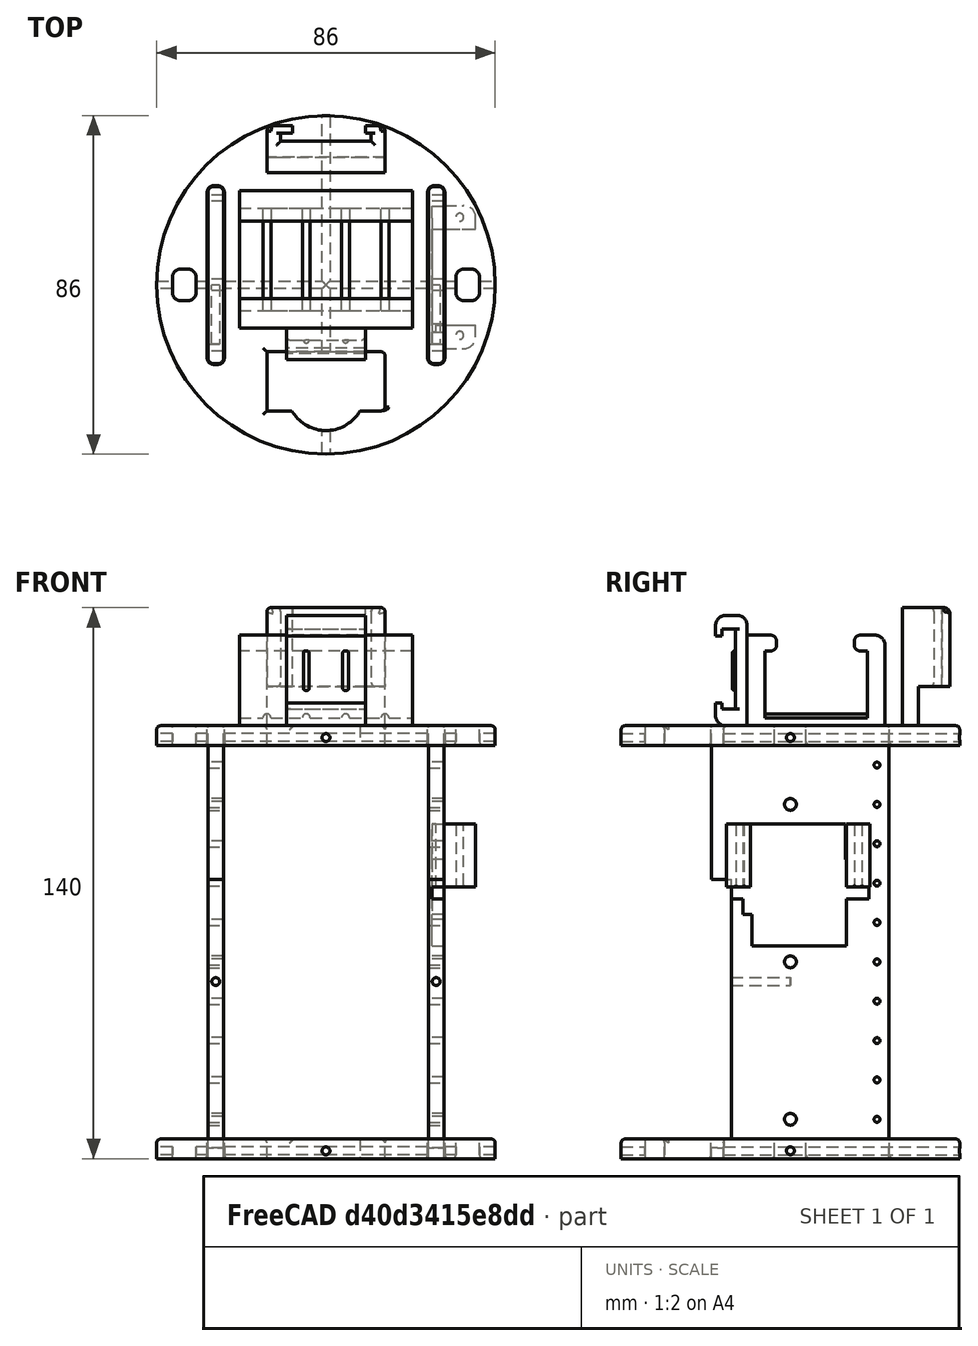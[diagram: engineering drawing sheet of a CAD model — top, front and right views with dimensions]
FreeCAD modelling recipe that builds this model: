
FCSTD DOCUMENT  (FreeCAD 1.0R39109 (Git))
Label: Base_inferior_capsula
License: All rights reserved
LicenseURL: http://en.wikipedia.org/wiki/All_rights_reserved
objects: Part::Cut×130, Part::Cylinder×98, Part::Fillet×96, Part::Box×72, Part::MultiFuse×37, Part::Offset×12, Part::Chamfer×1
note: 446 computed .brp shape members not serialized (recipe doc carries the construction recipe); baked Part::Feature solids carry a one-line shape summary decoded from their .brp

FEATURE [Part::Box] Box  label="Extensor"
  AttacherType = Attacher::AttachEngine3D
  Height = 66
  Length = 11
  Placement = pos=(30,-28,3) rot=(0,0,1;1.5708rad)
  Width = 60
FEATURE [Part::Box] Box001  label="Cubo001"
  AttacherType = Attacher::AttachEngine3D
  Height = 110
  Length = 45
  Placement = pos=(-30,25,0) rot=(0,0,-1;1.5708rad)
  Width = 4
FEATURE [Part::Box] Box002  label="Cubo002"
  AttacherType = Attacher::AttachEngine3D
  Height = 110
  Length = 45
  Placement = pos=(-30,25,0) rot=(0,0,-1;1.5708rad)
  Width = 4
FEATURE [Part::Box] Box003  label="Cubo003"
  AttacherType = Attacher::AttachEngine3D
  Height = 10
  Length = 30
  Placement = pos=(-15,-32,0) rot=(0,0,1;0rad)
  Width = 15
FEATURE [Part::Box] Box005  label="Cubo004"
  AttacherType = Attacher::AttachEngine3D
  Height = 15
  Length = 26
  Placement = pos=(-13,-23,110) rot=(0,0,1;0rad)
  Width = 35
FEATURE [Part::Box] Box006  label="Cubo005"
  AttacherType = Attacher::AttachEngine3D
  Height = 150
  Length = 6
  Width = 8
FEATURE [Part::Box] Box007  label="Cubo006"
  AttacherType = Attacher::AttachEngine3D
  Height = 150
  Length = 6
  Width = 8
FEATURE [Part::Box] Box008  label="Cubo007"
  AttacherType = Attacher::AttachEngine3D
  Height = 150
  Length = 6
  Width = 8
FEATURE [Part::Box] Box009  label="Cubo008"
  AttacherType = Attacher::AttachEngine3D
  Height = 150
  Length = 6
  Width = 8
FEATURE [Part::Box] Box010  label="Cubo009"
  AttacherType = Attacher::AttachEngine3D
  Height = 11.6
  Length = 20.8
  Placement = pos=(-10.5,-23,110) rot=(0,0,1;0rad)
  Width = 35
FEATURE [Part::Box] Box011  label="Cubo010"
  AttacherType = Attacher::AttachEngine3D
  Height = 11.6
  Length = 16
  Placement = pos=(-8,-23,116) rot=(0,0,1;0rad)
  Width = 35
FEATURE [Part::Box] Box095  label="Cubo095"
  AttacherType = Attacher::AttachEngine3D
  Height = 110
  Length = 45
  Placement = pos=(-30,25,0) rot=(0,0,-1;1.5708rad)
  Width = 4
FEATURE [Part::Box] Box096  label="Cubo096"
  AttacherType = Attacher::AttachEngine3D
  Height = 110
  Length = 45
  Placement = pos=(-30,25,0) rot=(0,0,-1;1.5708rad)
  Width = 4
FEATURE [Part::Box] Box097  label="Cubo097"
  AttacherType = Attacher::AttachEngine3D
  Height = 23
  Length = 24
  Width = 14
FEATURE [Part::Box] Box098  label="Cubo098"
  AttacherType = Attacher::AttachEngine3D
  Height = 3
  Length = 33.5
  Placement = pos=(-5,0,16) rot=(0,0,1;0rad)
  Width = 14
FEATURE [Part::Box] Box099  label="Cubo099"
  AttacherType = Attacher::AttachEngine3D
  Height = 1.4
  Length = 13
  Placement = pos=(9.8,5,28.6) rot=(0,0,1;0rad)
  Width = 4
FEATURE [Part::Box] Box100  label="Cubo100"
  AttacherType = Attacher::AttachEngine3D
  Height = 16
  Length = 10
  Placement = pos=(28,12.2,69) rot=(0,0,1;0rad)
  Width = 6
FEATURE [Part::Box] Box101  label="Cubo101"
  AttacherType = Attacher::AttachEngine3D
  Height = 16
  Length = 10
  Placement = pos=(28,-18.2,69) rot=(0,0,1;0rad)
  Width = 6
FEATURE [Part::Box] Box102  label="Extensor001"
  AttacherType = Attacher::AttachEngine3D
  Height = 66
  Length = 11
  Placement = pos=(30,-28,3) rot=(0,0,1;1.5708rad)
  Width = 60
FEATURE [Part::Box] Box104  label="Cubo102"
  AttacherType = Attacher::AttachEngine3D
  Height = 8
  Length = 20
  Width = 28
FEATURE [Part::Box] Box105  label="Cubo103"
  AttacherType = Attacher::AttachEngine3D
  Height = 2
  Length = 20.5
  Placement = pos=(0,4,4) rot=(0,0,1;0rad)
  Width = 20.5
FEATURE [Part::Box] Box106  label="Cubo104"
  AttacherType = Attacher::AttachEngine3D
  Height = 4
  Length = 20.5
  Placement = pos=(0,5,5) rot=(0,0,1;0rad)
  Width = 18.5
FEATURE [Part::Box] Box107  label="Cubo105"
  AttacherType = Attacher::AttachEngine3D
  Height = 8
  Length = 20
  Width = 30
FEATURE [Part::Box] Box108  label="Cubo106"
  AttacherType = Attacher::AttachEngine3D
  Height = 2
  Length = 20.5
  Placement = pos=(0,3.5,4) rot=(0,0,1;0rad)
  Width = 23
FEATURE [Part::Box] Box109  label="Cubo107"
  AttacherType = Attacher::AttachEngine3D
  Height = 4
  Length = 20.5
  Placement = pos=(0,5,5) rot=(0,0,1;0rad)
  Width = 18.5
FEATURE [Part::Box] Box110  label="Cubo108"
  AttacherType = Attacher::AttachEngine3D
  Height = 10
  Length = 20
  Placement = pos=(-9,-38,105) rot=(0,0,1;0rad)
  Width = 15
FEATURE [Part::Box] Box111  label="Cubo109"
  AttacherType = Attacher::AttachEngine3D
  Height = 110
  Length = 45
  Placement = pos=(-30,25,0) rot=(0,0,-1;1.5708rad)
  Width = 4
FEATURE [Part::Box] Box112  label="Extensor003"
  AttacherType = Attacher::AttachEngine3D
  Height = 66
  Length = 11
  Placement = pos=(30,-28,3) rot=(0,0,1;1.5708rad)
  Width = 60
FEATURE [Part::Box] Box113  label="Extensor004"
  AttacherType = Attacher::AttachEngine3D
  Height = 66
  Length = 11
  Placement = pos=(30,-28,3) rot=(0,0,1;1.5708rad)
  Width = 60
FEATURE [Part::Box] Box114  label="Cubo110"
  AttacherType = Attacher::AttachEngine3D
  Height = 110
  Length = 45
  Placement = pos=(-30,25,0) rot=(0,0,-1;1.5708rad)
  Width = 4
FEATURE [Part::Box] Box115  label="Cubo111"
  AttacherType = Attacher::AttachEngine3D
  Height = 23
  Length = 24
  Width = 14
FEATURE [Part::Box] Box116  label="Cubo112"
  AttacherType = Attacher::AttachEngine3D
  Height = 3
  Length = 33.5
  Placement = pos=(-5,0,16) rot=(0,0,1;0rad)
  Width = 14
FEATURE [Part::Box] Box117  label="Cubo113"
  AttacherType = Attacher::AttachEngine3D
  Height = 1.4
  Length = 13
  Placement = pos=(9.8,5,28.6) rot=(0,0,1;0rad)
  Width = 4
FEATURE [Part::Box] Box118  label="Cubo114"
  AttacherType = Attacher::AttachEngine3D
  Height = 16
  Length = 10
  Placement = pos=(28,12.2,69) rot=(0,0,1;0rad)
  Width = 6
FEATURE [Part::Box] Box119  label="Cubo115"
  AttacherType = Attacher::AttachEngine3D
  Height = 16
  Length = 10
  Placement = pos=(28,-18.2,69) rot=(0,0,1;0rad)
  Width = 6
FEATURE [Part::Box] Box120  label="Cubo116"
  AttacherType = Attacher::AttachEngine3D
  Height = 10
  Length = 4
  Placement = pos=(-30,-20,0) rot=(0,0,1;0rad)
  Width = 45
FEATURE [Part::Box] Box121  label="Cubo117"
  AttacherType = Attacher::AttachEngine3D
  Height = 10
  Length = 4
  Placement = pos=(-30,-20,0) rot=(0,0,1;0rad)
  Width = 45
FEATURE [Part::Box] Box122  label="Cubo118"
  AttacherType = Attacher::AttachEngine3D
  Height = 8
  Length = 20
  Width = 30
FEATURE [Part::Box] Box123  label="Cubo119"
  AttacherType = Attacher::AttachEngine3D
  Height = 2
  Length = 20.5
  Placement = pos=(0,3.5,4) rot=(0,0,1;0rad)
  Width = 23
FEATURE [Part::Box] Box124  label="Cubo120"
  AttacherType = Attacher::AttachEngine3D
  Height = 4
  Length = 20.5
  Placement = pos=(0,5,5) rot=(0,0,1;0rad)
  Width = 18.5
FEATURE [Part::Box] Box128  label="Cubo124"
  AttacherType = Attacher::AttachEngine3D
  Height = 30
  Length = 33
  Placement = pos=(-16,-43,115) rot=(0,0,1;0rad)
  Width = 30
FEATURE [Part::Box] Box129  label="Cubo125"
  AttacherType = Attacher::AttachEngine3D
  Height = 30
  Length = 33
  Placement = pos=(-16,13,110) rot=(0,0,1;0rad)
  Width = 30
FEATURE [Part::Box] Box130  label="Cubo126"
  AttacherType = Attacher::AttachEngine3D
  Height = 30
  Length = 30
  Placement = pos=(-16,13,110) rot=(0,0,1;0rad)
  Width = 4
FEATURE [Part::Box] Box131  label="Cubo127"
  AttacherType = Attacher::AttachEngine3D
  Height = 3.4
  Length = 21
  Placement = pos=(0,4.2,3) rot=(0,0,1;0rad)
  Width = 20.4
FEATURE [Part::Box] Box132  label="Cubo128"
  AttacherType = Attacher::AttachEngine3D
  Height = 4
  Length = 21
  Placement = pos=(0,5.75,6) rot=(0,0,1;0rad)
  Width = 17
FEATURE [Part::Box] Box133  label="Cubo129"
  AttacherType = Attacher::AttachEngine3D
  Height = 8
  Length = 20
  Width = 28
FEATURE [Part::Box] Box134  label="Cubo130"
  AttacherType = Attacher::AttachEngine3D
  Height = 16
  Length = 37
  Placement = pos=(-19,-15,110) rot=(0,0,1;0rad)
  Width = 30
FEATURE [Part::Box] Box135  label="Pila_ext"
  AttacherType = Attacher::AttachEngine3D
  Height = 25
  Length = 44
  Placement = pos=(-22,-11,110) rot=(0,0,1;0rad)
  Width = 35
FEATURE [Part::Box] Box136  label="Pila_int"
  AttacherType = Attacher::AttachEngine3D
  Height = 17
  Length = 44
  Placement = pos=(-22,-6.5,114) rot=(0,0,1;0rad)
  Width = 26
FEATURE [Part::Box] Box137  label="hueco_pila"
  AttacherType = Attacher::AttachEngine3D
  Height = 16.65
  Length = 44
  Placement = pos=(-22,-3.5,122) rot=(0,0,1;0rad)
  Width = 19.72
FEATURE [Part::Box] Box165  label="Cubo155"
  AttacherType = Attacher::AttachEngine3D
  Height = 17
  Length = 19
  Placement = pos=(27,-9.8,59) rot=(0,0,1;0rad)
  Width = 24
FEATURE [Part::Box] Box166  label="Cubo156"
  AttacherType = Attacher::AttachEngine3D
  Height = 66
  Length = 60
  Placement = pos=(-30,-20,5) rot=(0,0,1;0rad)
  Width = 5
FEATURE [Part::Box] Box167  label="Cubo157"
  AttacherType = Attacher::AttachEngine3D
  Height = 66
  Length = 60
  Placement = pos=(-30,-20,5) rot=(0,0,1;0rad)
  Width = 5
FEATURE [Part::Box] Box168  label="Cubo158"
  AttacherType = Attacher::AttachEngine3D
  Height = 3
  Length = 4
  Placement = pos=(27,7,66) rot=(0,0,1;0rad)
  Width = 13
FEATURE [Part::Box] Box169  label="Cubo159"
  AttacherType = Attacher::AttachEngine3D
  Height = 3
  Length = 4
  Placement = pos=(27,-9.8,56) rot=(0,0,1;0rad)
  Width = 24
FEATURE [Part::Box] Box170  label="Cubo160"
  AttacherType = Attacher::AttachEngine3D
  Height = 10
  Length = 30
  Placement = pos=(-15,-32,0) rot=(0,0,1;0rad)
  Width = 15
FEATURE [Part::Box] Box171  label="Cubo161"
  AttacherType = Attacher::AttachEngine3D
  Height = 150
  Length = 6
  Width = 8
FEATURE [Part::Box] Box172  label="Cubo162"
  AttacherType = Attacher::AttachEngine3D
  Height = 150
  Length = 6
  Width = 8
FEATURE [Part::Box] Box173  label="Cubo163"
  AttacherType = Attacher::AttachEngine3D
  Height = 110
  Length = 45
  Placement = pos=(-30,25,0) rot=(0,0,-1;1.5708rad)
  Width = 4
FEATURE [Part::Box] Box174  label="Extensor005"
  AttacherType = Attacher::AttachEngine3D
  Height = 66
  Length = 11
  Placement = pos=(30,-28,3) rot=(0,0,1;1.5708rad)
  Width = 60
FEATURE [Part::Box] Box175  label="Extensor006"
  AttacherType = Attacher::AttachEngine3D
  Height = 66
  Length = 11
  Placement = pos=(30,-28,3) rot=(0,0,1;1.5708rad)
  Width = 60
FEATURE [Part::Box] Box176  label="Cubo164"
  AttacherType = Attacher::AttachEngine3D
  Height = 110
  Length = 45
  Placement = pos=(-30,25,0) rot=(0,0,-1;1.5708rad)
  Width = 4
FEATURE [Part::Box] Box177  label="Cubo165"
  AttacherType = Attacher::AttachEngine3D
  Height = 23
  Length = 24
  Width = 14
FEATURE [Part::Box] Box178  label="Cubo166"
  AttacherType = Attacher::AttachEngine3D
  Height = 3
  Length = 33.5
  Placement = pos=(-5,0,16) rot=(0,0,1;0rad)
  Width = 14
FEATURE [Part::Box] Box179  label="Cubo167"
  AttacherType = Attacher::AttachEngine3D
  Height = 1.4
  Length = 13
  Placement = pos=(9.8,5,28.6) rot=(0,0,1;0rad)
  Width = 4
FEATURE [Part::Box] Box180  label="Cubo168"
  AttacherType = Attacher::AttachEngine3D
  Height = 16
  Length = 10
  Placement = pos=(28,12.2,69) rot=(0,0,1;0rad)
  Width = 6
FEATURE [Part::Box] Box181  label="Cubo169"
  AttacherType = Attacher::AttachEngine3D
  Height = 16
  Length = 10
  Placement = pos=(28,-18.2,69) rot=(0,0,1;0rad)
  Width = 6
FEATURE [Part::Box] Box182  label="Cubo170"
  AttacherType = Attacher::AttachEngine3D
  Height = 10
  Length = 4
  Placement = pos=(-30,-20,0) rot=(0,0,1;0rad)
  Width = 45
FEATURE [Part::Box] Box183  label="Cubo171"
  AttacherType = Attacher::AttachEngine3D
  Height = 10
  Length = 4
  Placement = pos=(-30,-20,0) rot=(0,0,1;0rad)
  Width = 45
FEATURE [Part::Box] Box184  label="Cubo172"
  AttacherType = Attacher::AttachEngine3D
  Height = 10
  Length = 120
  Placement = pos=(-50,-47,100) rot=(0,0,1;0rad)
  Width = 120
FEATURE [Part::Box] Box197  label="Cubo184"
  AttacherType = Attacher::AttachEngine3D
  Height = 16
  Length = 3
  Placement = pos=(27,12,69) rot=(0,0,1;0rad)
  Width = 2
FEATURE [Part::Box] Box198  label="Cubo185"
  AttacherType = Attacher::AttachEngine3D
  Height = 24
  Length = 3
  Placement = pos=(27,14.2,54) rot=(1,0,0;1.5708rad)
  Width = 4
FEATURE [Part::Cut] Cut016
  Base = -> Box005
  Tool = -> Box010
FEATURE [Part::Cut] Cut017
  Base = -> Cut016
  Placement = pos=(-5,0,0) rot=(0,0,1;1.5708rad)
  Tool = -> Box011
FEATURE [Part::Cut] Cut115
  Base = -> Box104
  Tool = -> Box105
FEATURE [Part::Cut] Cut116
  Base = -> Cut115
  Tool = -> Box106
FEATURE [Part::Cut] Cut117
  Base = -> Box107
  Tool = -> Box108
FEATURE [Part::Cut] Cut118
  Base = -> Cut117
  Tool = -> Box109
FEATURE [Part::Cut] Cut143
  Base = -> Box122
  Tool = -> Box123
FEATURE [Part::Cut] Cut144
  Base = -> Cut143
  Tool = -> Box124
FEATURE [Part::Cut] Cut149
  Base = -> Box133
  Tool = -> Box131
FEATURE [Part::Cut] Cut150
  Base = -> Cut149
  Tool = -> Box132
FEATURE [Part::Cut] Cut152
  Base = -> Box135
  Tool = -> Box136
FEATURE [Part::Cut] Cut153  label="PortaPIlas_9V"
  Base = -> Cut152
  Placement = pos=(0,0,-2) rot=(0,0,1;0rad)
  Tool = -> Box137
FEATURE [Part::Cylinder] Cylinder  label="Cilindro"
  Angle = 360
  AttacherType = Attacher::AttachEngine3D
  FirstAngle = 0
  Height = 5
  Radius = 43
  SecondAngle = 0
FEATURE [Part::Cylinder] Cylinder002  label="Cilindro002"
  Angle = 360
  AttacherType = Attacher::AttachEngine3D
  FirstAngle = 0
  Height = 20
  Placement = pos=(0,44,1.5) rot=(1,0,0;1.5708rad)
  Radius = 0.5
  SecondAngle = 0
FEATURE [Part::Cylinder] Cylinder003  label="Cilindro003"
  Angle = 360
  AttacherType = Attacher::AttachEngine3D
  FirstAngle = 0
  Height = 20
  Placement = pos=(0,-26,1.5) rot=(1,0,0;1.5708rad)
  Radius = 0.5
  SecondAngle = 0
FEATURE [Part::Cylinder] Cylinder004  label="Cilindro004"
  Angle = 360
  AttacherType = Attacher::AttachEngine3D
  FirstAngle = 0
  Height = 3
  Radius = 43
  SecondAngle = 0
FEATURE [Part::Cylinder] Cylinder005  label="Cilindro005"
  Angle = 360
  AttacherType = Attacher::AttachEngine3D
  FirstAngle = 0
  Height = 20
  Placement = pos=(0,44,1.5) rot=(1,0,0;1.5708rad)
  Radius = 0.5
  SecondAngle = 0
FEATURE [Part::Cylinder] Cylinder006  label="Cilindro006"
  Angle = 360
  AttacherType = Attacher::AttachEngine3D
  FirstAngle = 0
  Height = 20
  Placement = pos=(0,-26,1.5) rot=(1,0,0;1.5708rad)
  Radius = 0.5
  SecondAngle = 0
FEATURE [Part::Cylinder] Cylinder008  label="Cilindro008"
  Angle = 360
  AttacherType = Attacher::AttachEngine3D
  FirstAngle = 0
  Height = 100
  Placement = pos=(-46,0,50) rot=(0,1,0;1.5708rad)
  Radius = 1.5
  SecondAngle = 0
FEATURE [Part::Cylinder] Cylinder009  label="Cilindro009"
  Angle = 360
  AttacherType = Attacher::AttachEngine3D
  FirstAngle = 0
  Height = 100
  Placement = pos=(-46,0,90) rot=(0,1,0;1.5708rad)
  Radius = 1.5
  SecondAngle = 0
FEATURE [Part::Cylinder] Cylinder010  label="Cilindro010"
  Angle = 360
  AttacherType = Attacher::AttachEngine3D
  FirstAngle = 0
  Height = 100
  Placement = pos=(-46,0,10) rot=(0,1,0;1.5708rad)
  Radius = 1.5
  SecondAngle = 0
FEATURE [Part::Cylinder] Cylinder011  label="Cilindro011"
  Angle = 360
  AttacherType = Attacher::AttachEngine3D
  FirstAngle = 0
  Height = 10
  Placement = pos=(0,-27,0) rot=(0,0,1;0rad)
  Radius = 10
  SecondAngle = 0
FEATURE [Part::Cylinder] Cylinder071  label="Cilindro071"
  Angle = 360
  AttacherType = Attacher::AttachEngine3D
  FirstAngle = 0
  Height = 100
  Placement = pos=(-46,0,50) rot=(0,1,0;1.5708rad)
  Radius = 1.5
  SecondAngle = 0
FEATURE [Part::Cylinder] Cylinder072  label="Cilindro072"
  Angle = 360
  AttacherType = Attacher::AttachEngine3D
  FirstAngle = 0
  Height = 100
  Placement = pos=(-46,0,90) rot=(0,1,0;1.5708rad)
  Radius = 1.5
  SecondAngle = 0
FEATURE [Part::Cylinder] Cylinder073  label="Cilindro073"
  Angle = 360
  AttacherType = Attacher::AttachEngine3D
  FirstAngle = 0
  Height = 100
  Placement = pos=(-46,0,10) rot=(0,1,0;1.5708rad)
  Radius = 1.5
  SecondAngle = 0
FEATURE [Part::Cylinder] Cylinder074  label="Cilindro074"
  Angle = 360
  AttacherType = Attacher::AttachEngine3D
  FirstAngle = 0
  Height = 3
  Placement = pos=(7,7,23) rot=(0,0,1;0rad)
  Radius = 7
  SecondAngle = 0
FEATURE [Part::Cylinder] Cylinder075  label="Cilindro075"
  Angle = 360
  AttacherType = Attacher::AttachEngine3D
  FirstAngle = 0
  Height = 3
  Placement = pos=(14,7,23) rot=(0,0,1;0rad)
  Radius = 2
  SecondAngle = 0
FEATURE [Part::Cylinder] Cylinder076  label="Cilindro076"
  Angle = 360
  AttacherType = Attacher::AttachEngine3D
  FirstAngle = 0
  Height = 10
  Placement = pos=(-3.2,7,12) rot=(0,0,1;0rad)
  Radius = 1.65
  SecondAngle = 0
FEATURE [Part::Cylinder] Cylinder077  label="Cilindro077"
  Angle = 360
  AttacherType = Attacher::AttachEngine3D
  FirstAngle = 0
  Height = 10
  Placement = pos=(26.8,7,12) rot=(0,0,1;0rad)
  Radius = 1.65
  SecondAngle = 0
FEATURE [Part::Cylinder] Cylinder078  label="Cilindro078"
  Angle = 360
  AttacherType = Attacher::AttachEngine3D
  FirstAngle = 0
  Height = 4
  Placement = pos=(7,7,26) rot=(0,0,1;0rad)
  Radius = 3.5
  SecondAngle = 0
FEATURE [Part::Cylinder] Cylinder079  label="Cilindro079"
  Angle = 360
  AttacherType = Attacher::AttachEngine3D
  FirstAngle = 0
  Height = 10
  Placement = pos=(21,7,25) rot=(0,0,1;0rad)
  Radius = 0.25
  SecondAngle = 0
FEATURE [Part::Cylinder] Cylinder080  label="Cilindro080"
  Angle = 360
  AttacherType = Attacher::AttachEngine3D
  FirstAngle = 0
  Height = 10
  Placement = pos=(19,7,25) rot=(0,0,1;0rad)
  Radius = 0.25
  SecondAngle = 0
FEATURE [Part::Cylinder] Cylinder081  label="Cilindro081"
  Angle = 360
  AttacherType = Attacher::AttachEngine3D
  FirstAngle = 0
  Height = 10
  Placement = pos=(17,7,25) rot=(0,0,1;0rad)
  Radius = 0.25
  SecondAngle = 0
FEATURE [Part::Cylinder] Cylinder082  label="Cilindro082"
  Angle = 360
  AttacherType = Attacher::AttachEngine3D
  FirstAngle = 0
  Height = 10
  Placement = pos=(15,7,27) rot=(0,0,1;0rad)
  Radius = 0.25
  SecondAngle = 0
FEATURE [Part::Cylinder] Cylinder083  label="Cilindro083"
  Angle = 360
  AttacherType = Attacher::AttachEngine3D
  FirstAngle = 0
  Height = 10
  Placement = pos=(13,7,27) rot=(0,0,1;0rad)
  Radius = 0.25
  SecondAngle = 0
FEATURE [Part::Cylinder] Cylinder084  label="Cilindro084"
  Angle = 360
  AttacherType = Attacher::AttachEngine3D
  FirstAngle = 0
  Height = 20
  Placement = pos=(34,-14.8,66) rot=(0,0,1;0rad)
  Radius = 1
  SecondAngle = 0
FEATURE [Part::Cylinder] Cylinder085  label="Cilindro085"
  Angle = 360
  AttacherType = Attacher::AttachEngine3D
  FirstAngle = 0
  Height = 20
  Placement = pos=(34,15.2,66) rot=(0,0,1;0rad)
  Radius = 1
  SecondAngle = 0
FEATURE [Part::Cylinder] Cylinder086  label="Cilindro086"
  Angle = 360
  AttacherType = Attacher::AttachEngine3D
  FirstAngle = 0
  Height = 100
  Placement = pos=(-46,0,50) rot=(0,1,0;1.5708rad)
  Radius = 1.5
  SecondAngle = 0
FEATURE [Part::Cylinder] Cylinder087  label="Cilindro087"
  Angle = 360
  AttacherType = Attacher::AttachEngine3D
  FirstAngle = 0
  Height = 100
  Placement = pos=(-46,0,90) rot=(0,1,0;1.5708rad)
  Radius = 1.5
  SecondAngle = 0
FEATURE [Part::Cylinder] Cylinder088  label="Cilindro088"
  Angle = 360
  AttacherType = Attacher::AttachEngine3D
  FirstAngle = 0
  Height = 100
  Placement = pos=(-46,0,10) rot=(0,1,0;1.5708rad)
  Radius = 1.5
  SecondAngle = 0
FEATURE [Part::Cylinder] Cylinder089  label="Cilindro089"
  Angle = 360
  AttacherType = Attacher::AttachEngine3D
  FirstAngle = 0
  Height = 100
  Placement = pos=(-46,0,50) rot=(0,1,0;1.5708rad)
  Radius = 1.5
  SecondAngle = 0
FEATURE [Part::Cylinder] Cylinder090  label="Cilindro090"
  Angle = 360
  AttacherType = Attacher::AttachEngine3D
  FirstAngle = 0
  Height = 100
  Placement = pos=(-46,0,90) rot=(0,1,0;1.5708rad)
  Radius = 1.5
  SecondAngle = 0
FEATURE [Part::Cylinder] Cylinder091  label="Cilindro091"
  Angle = 360
  AttacherType = Attacher::AttachEngine3D
  FirstAngle = 0
  Height = 100
  Placement = pos=(-46,0,10) rot=(0,1,0;1.5708rad)
  Radius = 1.5
  SecondAngle = 0
FEATURE [Part::Cylinder] Cylinder092  label="Cilindro092"
  Angle = 360
  AttacherType = Attacher::AttachEngine3D
  FirstAngle = 0
  Height = 3
  Placement = pos=(7,7,23) rot=(0,0,1;0rad)
  Radius = 7
  SecondAngle = 0
FEATURE [Part::Cylinder] Cylinder093  label="Cilindro093"
  Angle = 360
  AttacherType = Attacher::AttachEngine3D
  FirstAngle = 0
  Height = 3
  Placement = pos=(14,7,23) rot=(0,0,1;0rad)
  Radius = 2
  SecondAngle = 0
FEATURE [Part::Cylinder] Cylinder094  label="Cilindro094"
  Angle = 360
  AttacherType = Attacher::AttachEngine3D
  FirstAngle = 0
  Height = 10
  Placement = pos=(-3.2,7,12) rot=(0,0,1;0rad)
  Radius = 1.65
  SecondAngle = 0
FEATURE [Part::Cylinder] Cylinder095  label="Cilindro095"
  Angle = 360
  AttacherType = Attacher::AttachEngine3D
  FirstAngle = 0
  Height = 10
  Placement = pos=(26.8,7,12) rot=(0,0,1;0rad)
  Radius = 1.65
  SecondAngle = 0
FEATURE [Part::Cylinder] Cylinder096  label="Cilindro096"
  Angle = 360
  AttacherType = Attacher::AttachEngine3D
  FirstAngle = 0
  Height = 4
  Placement = pos=(7,7,26) rot=(0,0,1;0rad)
  Radius = 3.5
  SecondAngle = 0
FEATURE [Part::Cylinder] Cylinder097  label="Cilindro097"
  Angle = 360
  AttacherType = Attacher::AttachEngine3D
  FirstAngle = 0
  Height = 10
  Placement = pos=(21,7,25) rot=(0,0,1;0rad)
  Radius = 0.25
  SecondAngle = 0
FEATURE [Part::Cylinder] Cylinder098  label="Cilindro098"
  Angle = 360
  AttacherType = Attacher::AttachEngine3D
  FirstAngle = 0
  Height = 10
  Placement = pos=(19,7,25) rot=(0,0,1;0rad)
  Radius = 0.25
  SecondAngle = 0
FEATURE [Part::Cylinder] Cylinder099  label="Cilindro099"
  Angle = 360
  AttacherType = Attacher::AttachEngine3D
  FirstAngle = 0
  Height = 10
  Placement = pos=(17,7,25) rot=(0,0,1;0rad)
  Radius = 0.25
  SecondAngle = 0
FEATURE [Part::Cylinder] Cylinder100  label="Cilindro100"
  Angle = 360
  AttacherType = Attacher::AttachEngine3D
  FirstAngle = 0
  Height = 10
  Placement = pos=(15,7,27) rot=(0,0,1;0rad)
  Radius = 0.25
  SecondAngle = 0
FEATURE [Part::Cylinder] Cylinder101  label="Cilindro101"
  Angle = 360
  AttacherType = Attacher::AttachEngine3D
  FirstAngle = 0
  Height = 10
  Placement = pos=(13,7,27) rot=(0,0,1;0rad)
  Radius = 0.25
  SecondAngle = 0
FEATURE [Part::Cylinder] Cylinder102  label="Cilindro102"
  Angle = 360
  AttacherType = Attacher::AttachEngine3D
  FirstAngle = 0
  Height = 20
  Placement = pos=(34,-14.8,66) rot=(0,0,1;0rad)
  Radius = 1
  SecondAngle = 0
FEATURE [Part::Cylinder] Cylinder103  label="Cilindro103"
  Angle = 360
  AttacherType = Attacher::AttachEngine3D
  FirstAngle = 0
  Height = 20
  Placement = pos=(34,15.2,66) rot=(0,0,1;0rad)
  Radius = 1
  SecondAngle = 0
FEATURE [Part::Cylinder] Cylinder104  label="Cilindro104"
  Angle = 360
  AttacherType = Attacher::AttachEngine3D
  FirstAngle = 0
  Height = 100
  Placement = pos=(0,52,2) rot=(1,0,0;1.5708rad)
  Radius = 1
  SecondAngle = 0
FEATURE [Part::Cylinder] Cylinder109  label="Cilindro109"
  Angle = 360
  AttacherType = Attacher::AttachEngine3D
  FirstAngle = 0
  Height = 15
  Placement = pos=(-28,0,45) rot=(1,0,0;1.5708rad)
  Radius = 1
  SecondAngle = 0
FEATURE [Part::Cylinder] Cylinder110  label="Cilindro110"
  Angle = 360
  AttacherType = Attacher::AttachEngine3D
  FirstAngle = 0
  Height = 15
  Placement = pos=(28,0,45) rot=(1,0,0;1.5708rad)
  Radius = 1
  SecondAngle = 0
FEATURE [Part::Cylinder] Cylinder111  label="Cilindro111"
  Angle = 360
  AttacherType = Attacher::AttachEngine3D
  FirstAngle = 0
  Height = 67
  Placement = pos=(-33,22,10) rot=(0,1,0;1.5708rad)
  Radius = 0.75
  SecondAngle = 0
FEATURE [Part::Cylinder] Cylinder112  label="Cilindro112"
  Angle = 360
  AttacherType = Attacher::AttachEngine3D
  FirstAngle = 0
  Height = 67
  Placement = pos=(-33,22,100) rot=(0,1,0;1.5708rad)
  Radius = 0.75
  SecondAngle = 0
FEATURE [Part::Cylinder] Cylinder113  label="Cilindro113"
  Angle = 360
  AttacherType = Attacher::AttachEngine3D
  FirstAngle = 0
  Height = 67
  Placement = pos=(-33,22,20) rot=(0,1,0;1.5708rad)
  Radius = 0.75
  SecondAngle = 0
FEATURE [Part::Cylinder] Cylinder114  label="Cilindro114"
  Angle = 360
  AttacherType = Attacher::AttachEngine3D
  FirstAngle = 0
  Height = 67
  Placement = pos=(-33,22,30) rot=(0,1,0;1.5708rad)
  Radius = 0.75
  SecondAngle = 0
FEATURE [Part::Cylinder] Cylinder115  label="Cilindro115"
  Angle = 360
  AttacherType = Attacher::AttachEngine3D
  FirstAngle = 0
  Height = 67
  Placement = pos=(-33,22,40) rot=(0,1,0;1.5708rad)
  Radius = 0.75
  SecondAngle = 0
FEATURE [Part::Cylinder] Cylinder116  label="Cilindro116"
  Angle = 360
  AttacherType = Attacher::AttachEngine3D
  FirstAngle = 0
  Height = 67
  Placement = pos=(-33,22,50) rot=(0,1,0;1.5708rad)
  Radius = 0.75
  SecondAngle = 0
FEATURE [Part::Cylinder] Cylinder117  label="Cilindro117"
  Angle = 360
  AttacherType = Attacher::AttachEngine3D
  FirstAngle = 0
  Height = 67
  Placement = pos=(-33,22,60) rot=(0,1,0;1.5708rad)
  Radius = 0.75
  SecondAngle = 0
FEATURE [Part::Cylinder] Cylinder118  label="Cilindro118"
  Angle = 360
  AttacherType = Attacher::AttachEngine3D
  FirstAngle = 0
  Height = 67
  Placement = pos=(-33,22,70) rot=(0,1,0;1.5708rad)
  Radius = 0.75
  SecondAngle = 0
FEATURE [Part::Cylinder] Cylinder119  label="Cilindro119"
  Angle = 360
  AttacherType = Attacher::AttachEngine3D
  FirstAngle = 0
  Height = 67
  Placement = pos=(-33,22,80) rot=(0,1,0;1.5708rad)
  Radius = 0.75
  SecondAngle = 0
FEATURE [Part::Cylinder] Cylinder120  label="Cilindro120"
  Angle = 360
  AttacherType = Attacher::AttachEngine3D
  FirstAngle = 0
  Height = 67
  Placement = pos=(-33,22,90) rot=(0,1,0;1.5708rad)
  Radius = 0.75
  SecondAngle = 0
FEATURE [Part::Cylinder] Cylinder121  label="Cilindro121"
  Angle = 360
  AttacherType = Attacher::AttachEngine3D
  FirstAngle = 0
  Height = 67
  Placement = pos=(-33,22,10) rot=(0,1,0;1.5708rad)
  Radius = 0.75
  SecondAngle = 0
FEATURE [Part::Cylinder] Cylinder122  label="Cilindro122"
  Angle = 360
  AttacherType = Attacher::AttachEngine3D
  FirstAngle = 0
  Height = 67
  Placement = pos=(-33,22,100) rot=(0,1,0;1.5708rad)
  Radius = 0.75
  SecondAngle = 0
FEATURE [Part::Cylinder] Cylinder123  label="Cilindro123"
  Angle = 360
  AttacherType = Attacher::AttachEngine3D
  FirstAngle = 0
  Height = 67
  Placement = pos=(-33,22,20) rot=(0,1,0;1.5708rad)
  Radius = 0.75
  SecondAngle = 0
FEATURE [Part::Cylinder] Cylinder124  label="Cilindro124"
  Angle = 360
  AttacherType = Attacher::AttachEngine3D
  FirstAngle = 0
  Height = 67
  Placement = pos=(-33,22,30) rot=(0,1,0;1.5708rad)
  Radius = 0.75
  SecondAngle = 0
FEATURE [Part::Cylinder] Cylinder125  label="Cilindro125"
  Angle = 360
  AttacherType = Attacher::AttachEngine3D
  FirstAngle = 0
  Height = 67
  Placement = pos=(-33,22,40) rot=(0,1,0;1.5708rad)
  Radius = 0.75
  SecondAngle = 0
FEATURE [Part::Cylinder] Cylinder126  label="Cilindro126"
  Angle = 360
  AttacherType = Attacher::AttachEngine3D
  FirstAngle = 0
  Height = 67
  Placement = pos=(-33,22,50) rot=(0,1,0;1.5708rad)
  Radius = 0.75
  SecondAngle = 0
FEATURE [Part::Cylinder] Cylinder127  label="Cilindro127"
  Angle = 360
  AttacherType = Attacher::AttachEngine3D
  FirstAngle = 0
  Height = 67
  Placement = pos=(-33,22,60) rot=(0,1,0;1.5708rad)
  Radius = 0.75
  SecondAngle = 0
FEATURE [Part::Cylinder] Cylinder128  label="Cilindro128"
  Angle = 360
  AttacherType = Attacher::AttachEngine3D
  FirstAngle = 0
  Height = 67
  Placement = pos=(-33,22,70) rot=(0,1,0;1.5708rad)
  Radius = 0.75
  SecondAngle = 0
FEATURE [Part::Cylinder] Cylinder129  label="Cilindro129"
  Angle = 360
  AttacherType = Attacher::AttachEngine3D
  FirstAngle = 0
  Height = 67
  Placement = pos=(-33,22,80) rot=(0,1,0;1.5708rad)
  Radius = 0.75
  SecondAngle = 0
FEATURE [Part::Cylinder] Cylinder130  label="Cilindro130"
  Angle = 360
  AttacherType = Attacher::AttachEngine3D
  FirstAngle = 0
  Height = 67
  Placement = pos=(-33,22,90) rot=(0,1,0;1.5708rad)
  Radius = 0.75
  SecondAngle = 0
FEATURE [Part::Cylinder] Cylinder131  label="Cilindro131"
  Angle = 360
  AttacherType = Attacher::AttachEngine3D
  FirstAngle = 0
  Height = 67
  Placement = pos=(-33,22,70) rot=(0,1,0;1.5708rad)
  Radius = 0.75
  SecondAngle = 0
FEATURE [Part::Cylinder] Cylinder133  label="Cilindro133"
  Angle = 360
  AttacherType = Attacher::AttachEngine3D
  FirstAngle = 0
  Height = 110
  Placement = pos=(-55,0,2) rot=(0.57735,0.57735,0.57735;2.0944rad)
  Radius = 1
  SecondAngle = 0
FEATURE [Part::Cylinder] Cylinder134  label="Cilindro134"
  Angle = 360
  AttacherType = Attacher::AttachEngine3D
  FirstAngle = 0
  Height = 5
  Radius = 43
  SecondAngle = 0
FEATURE [Part::Cylinder] Cylinder135  label="Cilindro135"
  Angle = 360
  AttacherType = Attacher::AttachEngine3D
  FirstAngle = 0
  Height = 20
  Placement = pos=(0,44,1.5) rot=(1,0,0;1.5708rad)
  Radius = 0.5
  SecondAngle = 0
FEATURE [Part::Cylinder] Cylinder136  label="Cilindro136"
  Angle = 360
  AttacherType = Attacher::AttachEngine3D
  FirstAngle = 0
  Height = 20
  Placement = pos=(0,-26,1.5) rot=(1,0,0;1.5708rad)
  Radius = 0.5
  SecondAngle = 0
FEATURE [Part::Cylinder] Cylinder137  label="Cilindro137"
  Angle = 360
  AttacherType = Attacher::AttachEngine3D
  FirstAngle = 0
  Height = 10
  Placement = pos=(0,-27,0) rot=(0,0,1;0rad)
  Radius = 10
  SecondAngle = 0
FEATURE [Part::Cylinder] Cylinder138  label="Cilindro138"
  Angle = 360
  AttacherType = Attacher::AttachEngine3D
  FirstAngle = 0
  Height = 100
  Placement = pos=(-46,0,50) rot=(0,1,0;1.5708rad)
  Radius = 1.5
  SecondAngle = 0
FEATURE [Part::Cylinder] Cylinder139  label="Cilindro139"
  Angle = 360
  AttacherType = Attacher::AttachEngine3D
  FirstAngle = 0
  Height = 100
  Placement = pos=(-46,0,90) rot=(0,1,0;1.5708rad)
  Radius = 1.5
  SecondAngle = 0
FEATURE [Part::Cylinder] Cylinder140  label="Cilindro140"
  Angle = 360
  AttacherType = Attacher::AttachEngine3D
  FirstAngle = 0
  Height = 100
  Placement = pos=(-46,0,10) rot=(0,1,0;1.5708rad)
  Radius = 1.5
  SecondAngle = 0
FEATURE [Part::Cylinder] Cylinder141  label="Cilindro141"
  Angle = 360
  AttacherType = Attacher::AttachEngine3D
  FirstAngle = 0
  Height = 100
  Placement = pos=(-46,0,50) rot=(0,1,0;1.5708rad)
  Radius = 1.5
  SecondAngle = 0
FEATURE [Part::Cylinder] Cylinder142  label="Cilindro142"
  Angle = 360
  AttacherType = Attacher::AttachEngine3D
  FirstAngle = 0
  Height = 100
  Placement = pos=(-46,0,90) rot=(0,1,0;1.5708rad)
  Radius = 1.5
  SecondAngle = 0
FEATURE [Part::Cylinder] Cylinder143  label="Cilindro143"
  Angle = 360
  AttacherType = Attacher::AttachEngine3D
  FirstAngle = 0
  Height = 100
  Placement = pos=(-46,0,10) rot=(0,1,0;1.5708rad)
  Radius = 1.5
  SecondAngle = 0
FEATURE [Part::Cylinder] Cylinder144  label="Cilindro144"
  Angle = 360
  AttacherType = Attacher::AttachEngine3D
  FirstAngle = 0
  Height = 3
  Placement = pos=(7,7,23) rot=(0,0,1;0rad)
  Radius = 7
  SecondAngle = 0
FEATURE [Part::Cylinder] Cylinder145  label="Cilindro145"
  Angle = 360
  AttacherType = Attacher::AttachEngine3D
  FirstAngle = 0
  Height = 3
  Placement = pos=(14,7,23) rot=(0,0,1;0rad)
  Radius = 2
  SecondAngle = 0
FEATURE [Part::Cylinder] Cylinder146  label="Cilindro146"
  Angle = 360
  AttacherType = Attacher::AttachEngine3D
  FirstAngle = 0
  Height = 10
  Placement = pos=(-3.2,7,12) rot=(0,0,1;0rad)
  Radius = 1.65
  SecondAngle = 0
FEATURE [Part::Cylinder] Cylinder147  label="Cilindro147"
  Angle = 360
  AttacherType = Attacher::AttachEngine3D
  FirstAngle = 0
  Height = 10
  Placement = pos=(26.8,7,12) rot=(0,0,1;0rad)
  Radius = 1.65
  SecondAngle = 0
FEATURE [Part::Cylinder] Cylinder148  label="Cilindro148"
  Angle = 360
  AttacherType = Attacher::AttachEngine3D
  FirstAngle = 0
  Height = 4
  Placement = pos=(7,7,26) rot=(0,0,1;0rad)
  Radius = 3.5
  SecondAngle = 0
FEATURE [Part::Cylinder] Cylinder149  label="Cilindro149"
  Angle = 360
  AttacherType = Attacher::AttachEngine3D
  FirstAngle = 0
  Height = 10
  Placement = pos=(21,7,25) rot=(0,0,1;0rad)
  Radius = 0.25
  SecondAngle = 0
FEATURE [Part::Cylinder] Cylinder150  label="Cilindro150"
  Angle = 360
  AttacherType = Attacher::AttachEngine3D
  FirstAngle = 0
  Height = 10
  Placement = pos=(19,7,25) rot=(0,0,1;0rad)
  Radius = 0.25
  SecondAngle = 0
FEATURE [Part::Cylinder] Cylinder151  label="Cilindro151"
  Angle = 360
  AttacherType = Attacher::AttachEngine3D
  FirstAngle = 0
  Height = 10
  Placement = pos=(17,7,25) rot=(0,0,1;0rad)
  Radius = 0.25
  SecondAngle = 0
FEATURE [Part::Cylinder] Cylinder152  label="Cilindro152"
  Angle = 360
  AttacherType = Attacher::AttachEngine3D
  FirstAngle = 0
  Height = 10
  Placement = pos=(15,7,27) rot=(0,0,1;0rad)
  Radius = 0.25
  SecondAngle = 0
FEATURE [Part::Cylinder] Cylinder153  label="Cilindro153"
  Angle = 360
  AttacherType = Attacher::AttachEngine3D
  FirstAngle = 0
  Height = 10
  Placement = pos=(13,7,27) rot=(0,0,1;0rad)
  Radius = 0.25
  SecondAngle = 0
FEATURE [Part::Cylinder] Cylinder154  label="Cilindro154"
  Angle = 360
  AttacherType = Attacher::AttachEngine3D
  FirstAngle = 0
  Height = 20
  Placement = pos=(34,-14.8,66) rot=(0,0,1;0rad)
  Radius = 1
  SecondAngle = 0
FEATURE [Part::Cylinder] Cylinder155  label="Cilindro155"
  Angle = 360
  AttacherType = Attacher::AttachEngine3D
  FirstAngle = 0
  Height = 20
  Placement = pos=(34,15.2,66) rot=(0,0,1;0rad)
  Radius = 1
  SecondAngle = 0
FEATURE [Part::Cylinder] Cylinder156  label="Cilindro156"
  Angle = 360
  AttacherType = Attacher::AttachEngine3D
  FirstAngle = 0
  Height = 100
  Placement = pos=(0,52,2) rot=(1,0,0;1.5708rad)
  Radius = 1
  SecondAngle = 0
FEATURE [Part::Cylinder] Cylinder157  label="Cilindro157"
  Angle = 360
  AttacherType = Attacher::AttachEngine3D
  FirstAngle = 0
  Height = 110
  Placement = pos=(-55,0,2) rot=(0.57735,0.57735,0.57735;2.0944rad)
  Radius = 1
  SecondAngle = 0
FEATURE [Part::Cylinder] Cylinder158  label="Cilindro158"
  Angle = 360
  AttacherType = Attacher::AttachEngine3D
  FirstAngle = 0
  Height = 29
  Placement = pos=(-15,22,112) rot=(1,0,0;1.5708rad)
  Radius = 1
  SecondAngle = 0
FEATURE [Part::Cylinder] Cylinder159  label="Cilindro159"
  Angle = 360
  AttacherType = Attacher::AttachEngine3D
  FirstAngle = 0
  Height = 29
  Placement = pos=(-5,22,112) rot=(1,0,0;1.5708rad)
  Radius = 1
  SecondAngle = 0
FEATURE [Part::Cylinder] Cylinder160  label="Cilindro160"
  Angle = 360
  AttacherType = Attacher::AttachEngine3D
  FirstAngle = 0
  Height = 29
  Placement = pos=(5,22,112) rot=(1,0,0;1.5708rad)
  Radius = 1
  SecondAngle = 0
FEATURE [Part::Cylinder] Cylinder161  label="Cilindro161"
  Angle = 360
  AttacherType = Attacher::AttachEngine3D
  FirstAngle = 0
  Height = 29
  Placement = pos=(15,22,112) rot=(1,0,0;1.5708rad)
  Radius = 1
  SecondAngle = 0
FEATURE [Part::Cylinder] Cylinder162  label="Cilindro162"
  Angle = 360
  AttacherType = Attacher::AttachEngine3D
  FirstAngle = 0
  Height = 10
  Placement = pos=(-5,-14,119) rot=(0,0,1;0rad)
  Radius = 0.75
  SecondAngle = 0
FEATURE [Part::Cylinder] Cylinder163  label="Cilindro163"
  Angle = 360
  AttacherType = Attacher::AttachEngine3D
  FirstAngle = 0
  Height = 10
  Placement = pos=(5,-14,119) rot=(0,0,1;0rad)
  Radius = 0.75
  SecondAngle = 0
FEATURE [Part::Fillet] Fillet
  Base = -> Cylinder
  EdgeLinks = -> Cylinder [Edge3]
  Edges = 1 edges r=1: [Edge3]
FEATURE [Part::Cut] Cut
  Base = -> Fillet
  Tool = -> Cylinder003
FEATURE [Part::Cut] Cut001  label="BaseInf"
  Base = -> Cut
  Tool = -> Cylinder002
FEATURE [Part::Cut] Cut093  label="BaseInf001"
  Base = -> Cut001
  Tool = -> Cylinder011
FEATURE [Part::Cut] Cut094  label="BaseInf002"
  Base = -> Cut093
  Tool = -> Box003
FEATURE [Part::Fillet] Fillet003
  Base = -> Cut118
  EdgeLinks = -> Cut118 [Edge23]
  Edges = 1 edges r=1: [Edge23]
FEATURE [Part::Fillet] Fillet004
  Base = -> Fillet003
  EdgeLinks = -> Fillet003 [Edge4]
  Edges = 1 edges r=1: [Edge4]
FEATURE [Part::Fillet] Fillet005  label="PortaSensor_Inclinacion001"
  Base = -> Fillet004
  EdgeLinks = -> Fillet004 [Edge34]
  Edges = 1 edges r=1: [Edge34]
  Placement = pos=(0,3.5,4) rot=(0,0,1;0rad)
FEATURE [Part::Fillet] Fillet006
  Base = -> Fillet005
  EdgeLinks = -> Fillet005 [Edge48]
  Edges = 1 edges r=1: [Edge48]
FEATURE [Part::Fillet] Fillet007  label="PortaSensor_TemHum"
  Base = -> Fillet006
  EdgeLinks = -> Fillet006 [Edge7,Edge18]
  Edges = 2 edges r=1: [Edge7,Edge18]
  Placement = pos=(-18,-9,137) rot=(0.57735,0.57735,-0.57735;2.0944rad)
FEATURE [Part::Fillet] Fillet009
  Base = -> Cylinder004
  EdgeLinks = -> Cylinder004 [Edge3]
  Edges = 1 edges r=1: [Edge3]
FEATURE [Part::Cut] Cut002
  Base = -> Fillet009
  Tool = -> Cylinder006
FEATURE [Part::Cut] Cut003
  Base = -> Cut002
  Placement = pos=(0,0,97) rot=(0,0,1;0rad)
  Tool = -> Cylinder005
FEATURE [Part::Fillet] Fillet010
  Base = -> Box001
  EdgeLinks = -> Box001 [Edge1,Edge3]
  Edges = 2 edges r=1.5: [Edge1,Edge3]
FEATURE [Part::Fillet] Fillet011  label="Lateral_Iz"
  Base = -> Fillet010
  EdgeLinks = -> Fillet010 [Edge17,Edge18]
  Edges = 2 edges r=1.5: [Edge17,Edge18]
FEATURE [Part::Fillet] Fillet012
  Base = -> Box002
  EdgeLinks = -> Box002 [Edge1,Edge3]
  Edges = 2 edges r=1.5: [Edge1,Edge3]
FEATURE [Part::Fillet] Fillet013  label="Lateral_De"
  Base = -> Fillet012
  EdgeLinks = -> Fillet012 [Edge17,Edge18]
  Edges = 2 edges r=1.5: [Edge17,Edge18]
  Placement = pos=(56,0,0) rot=(0,0,1;0rad)
FEATURE [Part::Fillet] Fillet019
  Base = -> Box006
  EdgeLinks = -> Box006 [Edge1,Edge3,Edge5,Edge7]
  Edges = 4 edges r=2: [Edge1,Edge3,Edge5,Edge7]
  Placement = pos=(-39,-4,0) rot=(0,0,1;0rad)
FEATURE [Part::Fillet] Fillet020
  Base = -> Box007
  EdgeLinks = -> Box007 [Edge1,Edge3,Edge5,Edge7]
  Edges = 4 edges r=2: [Edge1,Edge3,Edge5,Edge7]
  Placement = pos=(33,-4,0) rot=(0,0,1;0rad)
FEATURE [Part::Fillet] Fillet021
  Base = -> Box008
  EdgeLinks = -> Box008 [Edge1,Edge3,Edge5,Edge7]
  Edges = 4 edges r=2: [Edge1,Edge3,Edge5,Edge7]
  Placement = pos=(-39,-4,0) rot=(0,0,1;0rad)
FEATURE [Part::Cut] Cut095
  Base = -> Cut094
  Tool = -> Fillet021
FEATURE [Part::Cut] Cut096  label="BaseInf003"
  Base = -> Cut095
  Tool = -> Fillet020
FEATURE [Part::Fillet] Fillet022
  Base = -> Box009
  EdgeLinks = -> Box009 [Edge1,Edge3,Edge5,Edge7]
  Edges = 4 edges r=2: [Edge1,Edge3,Edge5,Edge7]
  Placement = pos=(33,-4,0) rot=(0,0,1;0rad)
FEATURE [Part::Fillet] Fillet032
  Base = -> Box095
  EdgeLinks = -> Box095 [Edge1,Edge3]
  Edges = 2 edges r=1.5: [Edge1,Edge3]
FEATURE [Part::Fillet] Fillet033  label="Lateral_De001"
  Base = -> Fillet032
  EdgeLinks = -> Fillet032 [Edge17,Edge18]
  Edges = 2 edges r=1.5: [Edge17,Edge18]
  Placement = pos=(56,0,0) rot=(0,0,1;0rad)
FEATURE [Part::Cut] Cut100
  Base = -> Fillet033
  Tool = -> Cylinder010
FEATURE [Part::Cut] Cut101
  Base = -> Cut100
  Tool = -> Cylinder009
FEATURE [Part::Cut] Cut102
  Base = -> Cut101
  Tool = -> Cylinder008
FEATURE [Part::Fillet] Fillet034
  Base = -> Box096
  EdgeLinks = -> Box096 [Edge1,Edge3]
  Edges = 2 edges r=1.5: [Edge1,Edge3]
FEATURE [Part::Fillet] Fillet035  label="Lateral_Iz001"
  Base = -> Fillet034
  EdgeLinks = -> Fillet034 [Edge17,Edge18]
  Edges = 2 edges r=1.5: [Edge17,Edge18]
FEATURE [Part::Cut] Cut097
  Base = -> Fillet035
  Tool = -> Cylinder071
FEATURE [Part::Cut] Cut098
  Base = -> Cut097
  Tool = -> Cylinder073
FEATURE [Part::Cut] Cut099  label="Lateral_Iz002"
  Base = -> Cut098
  Tool = -> Cylinder072
FEATURE [Part::Fillet] Fillet039
  Base = -> Box100
  EdgeLinks = -> Box100 [Edge7]
  Edges = 1 edges r=3: [Edge7]
FEATURE [Part::Cut] Cut112
  Base = -> Fillet039
  Tool = -> Cylinder085
FEATURE [Part::Fillet] Fillet040
  Base = -> Box101
  EdgeLinks = -> Box101 [Edge5]
  Edges = 1 edges r=3: [Edge5]
FEATURE [Part::Cut] Cut111
  Base = -> Fillet040
  Tool = -> Cylinder084
FEATURE [Part::Fillet] Fillet041
  Base = -> Cut111
  EdgeLinks = -> Cut111 [Edge15]
  Edges = 1 edges r=0.5: [Edge15]
  Placement = pos=(0,2,0) rot=(0,0,1;0rad)
FEATURE [Part::Fillet] Fillet042
  Base = -> Cut112
  EdgeLinks = -> Cut112 [Edge15]
  Edges = 1 edges r=0.5: [Edge15]
  Placement = pos=(0,2,0) rot=(0,0,1;0rad)
FEATURE [Part::Fillet] Fillet043
  Base = -> Cut116
  EdgeLinks = -> Cut116 [Edge23]
  Edges = 1 edges r=1: [Edge23]
FEATURE [Part::Fillet] Fillet001
  Base = -> Fillet043
  EdgeLinks = -> Fillet043 [Edge4]
  Edges = 1 edges r=1: [Edge4]
FEATURE [Part::Fillet] Fillet002  label="PortaSensor"
  Base = -> Fillet001
  EdgeLinks = -> Fillet001 [Edge34]
  Edges = 1 edges r=1: [Edge34]
  Placement = pos=(-12,11,110) rot=(0,0,1;0rad)
FEATURE [Part::Fillet] Fillet044
  Base = -> Fillet002
  EdgeLinks = -> Fillet002 [Edge48]
  Edges = 1 edges r=1: [Edge48]
FEATURE [Part::Fillet] Fillet045
  Base = -> Fillet044
  EdgeLinks = -> Fillet044 [Edge18]
  Edges = 1 edges r=1: [Edge18]
FEATURE [Part::Fillet] Fillet046
  Base = -> Fillet045
  EdgeLinks = -> Fillet045 [Edge22]
  Edges = 1 edges r=1: [Edge22]
FEATURE [Part::Fillet] Fillet049
  Base = -> Box110
  EdgeLinks = -> Box110 [Edge1,Edge3,Edge5,Edge7]
  Edges = 4 edges r=6: [Edge1,Edge3,Edge5,Edge7]
FEATURE [Part::Fillet] Fillet051
  Base = -> Box111
  EdgeLinks = -> Box111 [Edge1,Edge3]
  Edges = 2 edges r=1.5: [Edge1,Edge3]
FEATURE [Part::Fillet] Fillet052  label="Lateral_Iz006"
  Base = -> Fillet051
  EdgeLinks = -> Fillet051 [Edge17,Edge18]
  Edges = 2 edges r=1.5: [Edge17,Edge18]
FEATURE [Part::Cut] Cut120
  Base = -> Fillet052
  Tool = -> Cylinder086
FEATURE [Part::Cut] Cut121
  Base = -> Cut120
  Tool = -> Cylinder088
FEATURE [Part::Cut] Cut122  label="Lateral_Iz004"
  Base = -> Cut121
  Tool = -> Cylinder087
FEATURE [Part::Fillet] Fillet053
  Base = -> Box114
  EdgeLinks = -> Box114 [Edge1,Edge3]
  Edges = 2 edges r=1.5: [Edge1,Edge3]
FEATURE [Part::Fillet] Fillet054  label="Lateral_De005"
  Base = -> Fillet053
  EdgeLinks = -> Fillet053 [Edge17,Edge18]
  Edges = 2 edges r=1.5: [Edge17,Edge18]
  Placement = pos=(56,0,0) rot=(0,0,1;0rad)
FEATURE [Part::Cut] Cut124
  Base = -> Fillet054
  Tool = -> Cylinder091
FEATURE [Part::Cut] Cut125
  Base = -> Cut124
  Tool = -> Cylinder090
FEATURE [Part::Cut] Cut126
  Base = -> Cut125
  Tool = -> Cylinder089
FEATURE [Part::Fillet] Fillet058
  Base = -> Box118
  EdgeLinks = -> Box118 [Edge7]
  Edges = 1 edges r=3: [Edge7]
FEATURE [Part::Cut] Cut136
  Base = -> Fillet058
  Tool = -> Cylinder103
FEATURE [Part::Fillet] Fillet059
  Base = -> Box119
  EdgeLinks = -> Box119 [Edge5]
  Edges = 1 edges r=3: [Edge5]
FEATURE [Part::Cut] Cut135
  Base = -> Fillet059
  Tool = -> Cylinder102
FEATURE [Part::Fillet] Fillet060
  Base = -> Cut135
  EdgeLinks = -> Cut135 [Edge15]
  Edges = 1 edges r=0.5: [Edge15]
  Placement = pos=(0,2,0) rot=(0,0,1;0rad)
FEATURE [Part::Fillet] Fillet061
  Base = -> Cut136
  EdgeLinks = -> Cut136 [Edge15]
  Edges = 1 edges r=0.5: [Edge15]
  Placement = pos=(0,2,0) rot=(0,0,1;0rad)
FEATURE [Part::Fillet] Fillet062
  Base = -> Box120
  EdgeLinks = -> Box120 [Edge3,Edge7]
  Edges = 2 edges r=1.5: [Edge3,Edge7]
FEATURE [Part::Fillet] Fillet063
  Base = -> Fillet062
  EdgeLinks = -> Fillet062 [Edge2,Edge13]
  Edges = 2 edges r=1.5: [Edge2,Edge13]
  Placement = pos=(0,0,-3) rot=(0,0,1;0rad)
FEATURE [Part::Fillet] Fillet064
  Base = -> Box121
  EdgeLinks = -> Box121 [Edge3,Edge7]
  Edges = 2 edges r=1.5: [Edge3,Edge7]
FEATURE [Part::Fillet] Fillet065
  Base = -> Fillet064
  EdgeLinks = -> Fillet064 [Edge2,Edge13]
  Edges = 2 edges r=1.5: [Edge2,Edge13]
  Placement = pos=(0,0,-3) rot=(0,0,1;0rad)
FEATURE [Part::Fillet] Fillet069
  Base = -> Cut144
  EdgeLinks = -> Cut144 [Edge23]
  Edges = 1 edges r=1: [Edge23]
FEATURE [Part::Fillet] Fillet070
  Base = -> Fillet069
  EdgeLinks = -> Fillet069 [Edge4]
  Edges = 1 edges r=1: [Edge4]
FEATURE [Part::Fillet] Fillet071  label="PortaSensor_Inclinacion002"
  Base = -> Fillet070
  EdgeLinks = -> Fillet070 [Edge34]
  Edges = 1 edges r=1: [Edge34]
  Placement = pos=(0,3.5,4) rot=(0,0,1;0rad)
FEATURE [Part::Fillet] Fillet072
  Base = -> Fillet071
  EdgeLinks = -> Fillet071 [Edge48]
  Edges = 1 edges r=1: [Edge48]
FEATURE [Part::Fillet] Fillet073  label="PortaSensor_TemHum001"
  Base = -> Fillet072
  EdgeLinks = -> Fillet072 [Edge7,Edge18]
  Edges = 2 edges r=1: [Edge7,Edge18]
  Placement = pos=(17.5,13,140) rot=(0.57735,-0.57735,-0.57735;4.18879rad)
FEATURE [Part::Fillet] Fillet081
  Base = -> Cut150
  EdgeLinks = -> Cut150 [Edge23]
  Edges = 1 edges r=1: [Edge23]
FEATURE [Part::Fillet] Fillet082  label="PortaSensor_Inclinación"
  Base = -> Fillet081
  EdgeLinks = -> Fillet081 [Edge8]
  Edges = 1 edges r=1: [Edge8]
  Placement = pos=(-10,-11,110) rot=(1,0,0;1.5708rad)
FEATURE [Part::Fillet] Fillet083
  Base = -> Cut153
  EdgeLinks = -> Cut153 [Edge13,Edge29]
  Edges = 2 edges r=1.5: [Edge13,Edge29]
FEATURE [Part::Fillet] Fillet084  label="PortaPilas_9V"
  Base = -> Fillet083
  EdgeLinks = -> Fillet083 [Edge23,Edge41]
  Edges = 2 edges r=1.5: [Edge23,Edge41]
FEATURE [Part::Fillet] Fillet120
  Base = -> Cylinder134
  EdgeLinks = -> Cylinder134 [Edge3]
  Edges = 1 edges r=1: [Edge3]
FEATURE [Part::Cut] Cut205
  Base = -> Fillet120
  Tool = -> Cylinder136
FEATURE [Part::Cut] Cut206  label="BaseInf010"
  Base = -> Cut205
  Tool = -> Cylinder135
FEATURE [Part::Cut] Cut207  label="BaseInf011"
  Base = -> Cut206
  Tool = -> Cylinder137
FEATURE [Part::Cut] Cut208  label="BaseInf012"
  Base = -> Cut207
  Tool = -> Box170
FEATURE [Part::Fillet] Fillet121
  Base = -> Box171
  EdgeLinks = -> Box171 [Edge1,Edge3,Edge5,Edge7]
  Edges = 4 edges r=2: [Edge1,Edge3,Edge5,Edge7]
  Placement = pos=(33,-4,0) rot=(0,0,1;0rad)
FEATURE [Part::Fillet] Fillet122
  Base = -> Box172
  EdgeLinks = -> Box172 [Edge1,Edge3,Edge5,Edge7]
  Edges = 4 edges r=2: [Edge1,Edge3,Edge5,Edge7]
  Placement = pos=(-39,-4,0) rot=(0,0,1;0rad)
FEATURE [Part::Cut] Cut209
  Base = -> Cut208
  Tool = -> Fillet122
FEATURE [Part::Cut] Cut210  label="BaseInf013"
  Base = -> Cut209
  Tool = -> Fillet121
FEATURE [Part::Fillet] Fillet123
  Base = -> Box173
  EdgeLinks = -> Box173 [Edge1,Edge3]
  Edges = 2 edges r=1.5: [Edge1,Edge3]
FEATURE [Part::Fillet] Fillet124  label="Lateral_Iz010"
  Base = -> Fillet123
  EdgeLinks = -> Fillet123 [Edge17,Edge18]
  Edges = 2 edges r=1.5: [Edge17,Edge18]
FEATURE [Part::Cut] Cut211
  Base = -> Fillet124
  Tool = -> Cylinder138
FEATURE [Part::Cut] Cut212
  Base = -> Cut211
  Tool = -> Cylinder140
FEATURE [Part::Cut] Cut213  label="Lateral_Iz008"
  Base = -> Cut212
  Tool = -> Cylinder139
FEATURE [Part::Fillet] Fillet125
  Base = -> Box176
  EdgeLinks = -> Box176 [Edge1,Edge3]
  Edges = 2 edges r=1.5: [Edge1,Edge3]
FEATURE [Part::Fillet] Fillet126  label="Lateral_De009"
  Base = -> Fillet125
  EdgeLinks = -> Fillet125 [Edge17,Edge18]
  Edges = 2 edges r=1.5: [Edge17,Edge18]
  Placement = pos=(56,0,0) rot=(0,0,1;0rad)
FEATURE [Part::Cut] Cut215
  Base = -> Fillet126
  Tool = -> Cylinder143
FEATURE [Part::Cut] Cut216
  Base = -> Cut215
  Tool = -> Cylinder142
FEATURE [Part::Cut] Cut217
  Base = -> Cut216
  Tool = -> Cylinder141
FEATURE [Part::Fillet] Fillet130
  Base = -> Box180
  EdgeLinks = -> Box180 [Edge7]
  Edges = 1 edges r=3: [Edge7]
FEATURE [Part::Cut] Cut227
  Base = -> Fillet130
  Tool = -> Cylinder155
FEATURE [Part::Fillet] Fillet131
  Base = -> Box181
  EdgeLinks = -> Box181 [Edge5]
  Edges = 1 edges r=3: [Edge5]
FEATURE [Part::Cut] Cut226
  Base = -> Fillet131
  Tool = -> Cylinder154
FEATURE [Part::Fillet] Fillet132
  Base = -> Cut226
  EdgeLinks = -> Cut226 [Edge15]
  Edges = 1 edges r=0.5: [Edge15]
  Placement = pos=(0,2,0) rot=(0,0,1;0rad)
FEATURE [Part::Fillet] Fillet133
  Base = -> Cut227
  EdgeLinks = -> Cut227 [Edge15]
  Edges = 1 edges r=0.5: [Edge15]
  Placement = pos=(0,2,0) rot=(0,0,1;0rad)
FEATURE [Part::Fillet] Fillet134
  Base = -> Box182
  EdgeLinks = -> Box182 [Edge3,Edge7]
  Edges = 2 edges r=1.5: [Edge3,Edge7]
FEATURE [Part::Fillet] Fillet135
  Base = -> Fillet134
  EdgeLinks = -> Fillet134 [Edge2,Edge13]
  Edges = 2 edges r=1.5: [Edge2,Edge13]
  Placement = pos=(0,0,-3) rot=(0,0,1;0rad)
FEATURE [Part::Fillet] Fillet136
  Base = -> Box183
  EdgeLinks = -> Box183 [Edge3,Edge7]
  Edges = 2 edges r=1.5: [Edge3,Edge7]
FEATURE [Part::Fillet] Fillet137
  Base = -> Fillet136
  EdgeLinks = -> Fillet136 [Edge2,Edge13]
  Edges = 2 edges r=1.5: [Edge2,Edge13]
  Placement = pos=(0,0,-3) rot=(0,0,1;0rad)
FEATURE [Part::Fillet] Fillet145
  Base = -> Cylinder162
  EdgeLinks = -> Cylinder162 [Edge3]
  Edges = 1 edges r=0.5: [Edge3]
FEATURE [Part::Fillet] Fillet146
  Base = -> Fillet145
  EdgeLinks = -> Fillet145 [Edge3]
  Edges = 1 edges r=0.5: [Edge3]
FEATURE [Part::Fillet] Fillet147
  Base = -> Cylinder163
  EdgeLinks = -> Cylinder163 [Edge3]
  Edges = 1 edges r=0.5: [Edge3]
FEATURE [Part::Fillet] Fillet148
  Base = -> Fillet147
  EdgeLinks = -> Fillet147 [Edge3]
  Edges = 1 edges r=0.5: [Edge3]
FEATURE [Part::MultiFuse] Fusion069
  Shapes = -> [Cylinder074,Cylinder075]
FEATURE [Part::MultiFuse] Fusion070
  Shapes = -> [Box097,Fusion069]
FEATURE [Part::MultiFuse] Fusion071
  Shapes = -> [Fusion070,Box098]
FEATURE [Part::Cut] Cut103
  Base = -> Fusion071
  Tool = -> Cylinder076
FEATURE [Part::Cut] Cut104  label="Servo002"
  Base = -> Cut103
  Tool = -> Cylinder077
FEATURE [Part::MultiFuse] Fusion072
  Shapes = -> [Cylinder078,Box099]
FEATURE [Part::Fillet] Fillet036
  Base = -> Fusion072
  EdgeLinks = -> Fusion072 [Edge4]
  Edges = 1 edges r=2: [Edge4]
FEATURE [Part::Fillet] Fillet037
  Base = -> Fillet036
  EdgeLinks = -> Fillet036 [Edge25]
  Edges = 1 edges r=1: [Edge25]
FEATURE [Part::Fillet] Fillet038
  Base = -> Fillet037
  EdgeLinks = -> Fillet037 [Edge17]
  Edges = 1 edges r=1: [Edge17]
FEATURE [Part::MultiFuse] Fusion073
  Shapes = -> [Cut104,Fillet038]
FEATURE [Part::Cut] Cut105
  Base = -> Fusion073
  Tool = -> Cylinder079
FEATURE [Part::Cut] Cut106
  Base = -> Cut105
  Tool = -> Cylinder083
FEATURE [Part::Cut] Cut107
  Base = -> Cut106
  Tool = -> Cylinder082
FEATURE [Part::Cut] Cut108
  Base = -> Cut107
  Tool = -> Cylinder081
FEATURE [Part::Cut] Cut109  label="Servo003"
  Base = -> Cut108
  Placement = pos=(41,12,85) rot=(0.707107,-0.707107,0;3.14159rad)
  Tool = -> Cylinder080
FEATURE [Part::Cut] Cut110
  Base = -> Cut102
  Tool = -> Cut109
FEATURE [Part::MultiFuse] Fusion
  Shapes = -> [Cut110,Fillet041]
FEATURE [Part::MultiFuse] Fusion074  label="Lateral_De002"
  Shapes = -> [Fusion,Fillet042]
FEATURE [Part::MultiFuse] Fusion078
  Shapes = -> [Cylinder092,Cylinder093]
FEATURE [Part::MultiFuse] Fusion079
  Shapes = -> [Box115,Fusion078]
FEATURE [Part::MultiFuse] Fusion080
  Shapes = -> [Fusion079,Box116]
FEATURE [Part::Cut] Cut127
  Base = -> Fusion080
  Tool = -> Cylinder094
FEATURE [Part::Cut] Cut128  label="Servo004"
  Base = -> Cut127
  Tool = -> Cylinder095
FEATURE [Part::MultiFuse] Fusion081
  Shapes = -> [Cylinder096,Box117]
FEATURE [Part::Fillet] Fillet055
  Base = -> Fusion081
  EdgeLinks = -> Fusion081 [Edge4]
  Edges = 1 edges r=2: [Edge4]
FEATURE [Part::Fillet] Fillet056
  Base = -> Fillet055
  EdgeLinks = -> Fillet055 [Edge25]
  Edges = 1 edges r=1: [Edge25]
FEATURE [Part::Fillet] Fillet057
  Base = -> Fillet056
  EdgeLinks = -> Fillet056 [Edge17]
  Edges = 1 edges r=1: [Edge17]
FEATURE [Part::MultiFuse] Fusion082
  Shapes = -> [Cut128,Fillet057]
FEATURE [Part::Cut] Cut129
  Base = -> Fusion082
  Tool = -> Cylinder097
FEATURE [Part::Cut] Cut130
  Base = -> Cut129
  Tool = -> Cylinder101
FEATURE [Part::Cut] Cut131
  Base = -> Cut130
  Tool = -> Cylinder100
FEATURE [Part::Cut] Cut132
  Base = -> Cut131
  Tool = -> Cylinder099
FEATURE [Part::Cut] Cut133  label="Servo005"
  Base = -> Cut132
  Placement = pos=(41,12,85) rot=(0.707107,-0.707107,0;3.14159rad)
  Tool = -> Cylinder098
FEATURE [Part::Cut] Cut134
  Base = -> Cut126
  Tool = -> Cut133
FEATURE [Part::MultiFuse] Fusion077
  Shapes = -> [Cut134,Fillet060]
FEATURE [Part::MultiFuse] Fusion083  label="Lateral_De006"
  Shapes = -> [Fusion077,Fillet061]
FEATURE [Part::MultiFuse] Fusion084
  Shapes = -> [Fillet073,Box130]
FEATURE [Part::Fillet] Fillet077
  Base = -> Fusion084
  EdgeLinks = -> Fusion084 [Edge2,Edge16]
  Edges = 2 edges r=1: [Edge2,Edge16]
FEATURE [Part::Fillet] Fillet078  label="PortaSensor_TemHum002"
  Base = -> Fillet077
  EdgeLinks = -> Fillet077 [Edge20,Edge56]
  Edges = 2 edges r=1: [Edge20,Edge56]
FEATURE [Part::Fillet] Fillet079
  Base = -> Fillet078
  EdgeLinks = -> Fillet078 [Edge45]
  Edges = 1 edges r=1.5: [Edge45]
FEATURE [Part::Fillet] Fillet080  label="PortaSensor_TemHum003"
  Base = -> Fillet079
  EdgeLinks = -> Fillet079 [Edge39]
  Edges = 1 edges r=1.5: [Edge39]
  Placement = pos=(1,15.5,0) rot=(0,0,1;0rad)
FEATURE [Part::MultiFuse] Fusion097
  Shapes = -> [Cylinder144,Cylinder145]
FEATURE [Part::MultiFuse] Fusion098
  Shapes = -> [Box177,Fusion097]
FEATURE [Part::MultiFuse] Fusion099
  Shapes = -> [Fusion098,Box178]
FEATURE [Part::Cut] Cut218
  Base = -> Fusion099
  Tool = -> Cylinder146
FEATURE [Part::Cut] Cut219  label="Servo006"
  Base = -> Cut218
  Tool = -> Cylinder147
FEATURE [Part::MultiFuse] Fusion100
  Shapes = -> [Cylinder148,Box179]
FEATURE [Part::Fillet] Fillet127
  Base = -> Fusion100
  EdgeLinks = -> Fusion100 [Edge4]
  Edges = 1 edges r=2: [Edge4]
FEATURE [Part::Fillet] Fillet128
  Base = -> Fillet127
  EdgeLinks = -> Fillet127 [Edge25]
  Edges = 1 edges r=1: [Edge25]
FEATURE [Part::Fillet] Fillet129
  Base = -> Fillet128
  EdgeLinks = -> Fillet128 [Edge17]
  Edges = 1 edges r=1: [Edge17]
FEATURE [Part::MultiFuse] Fusion101
  Shapes = -> [Cut219,Fillet129]
FEATURE [Part::Cut] Cut220
  Base = -> Fusion101
  Tool = -> Cylinder149
FEATURE [Part::Cut] Cut221
  Base = -> Cut220
  Tool = -> Cylinder153
FEATURE [Part::Cut] Cut222
  Base = -> Cut221
  Tool = -> Cylinder152
FEATURE [Part::Cut] Cut223
  Base = -> Cut222
  Tool = -> Cylinder151
FEATURE [Part::Cut] Cut224  label="Servo007"
  Base = -> Cut223
  Placement = pos=(41,12,85) rot=(0.707107,-0.707107,0;3.14159rad)
  Tool = -> Cylinder150
FEATURE [Part::Cut] Cut225
  Base = -> Cut217
  Tool = -> Cut224
FEATURE [Part::MultiFuse] Fusion096
  Shapes = -> [Cut225,Fillet132]
FEATURE [Part::MultiFuse] Fusion102  label="Lateral_De010"
  Shapes = -> [Fusion096,Fillet133]
FEATURE [Part::Offset] Offset
  Fill = false
  Intersection = false
  Join = 0
  Mode = 0
  SelfIntersection = false
  Source = -> Fillet011
  Value = 0.2
FEATURE [Part::Cut] Cut004
  Base = -> Cut003
  Tool = -> Offset
FEATURE [Part::Offset] Offset001
  Fill = false
  Intersection = false
  Join = 0
  Mode = 0
  SelfIntersection = false
  Source = -> Fillet013
  Value = 0.2
FEATURE [Part::Cut] Cut005  label="Base_2"
  Base = -> Cut004
  Placement = pos=(0,0,10) rot=(0,0,1;0rad)
  Tool = -> Offset001
FEATURE [Part::Cut] Cut012
  Base = -> Cut005
  Tool = -> Fillet019
FEATURE [Part::Cut] Cut013
  Base = -> Cut012
  Tool = -> Fillet022
FEATURE [Part::MultiFuse] Fusion002  label="BaseSup"
  Shapes = -> [Cut013,Cut017]
FEATURE [Part::MultiFuse] Fusion075  label="BaseSup001"
  Shapes = -> [Fusion002,Fillet046]
FEATURE [Part::Fillet] Fillet047
  Base = -> Fusion075
  EdgeLinks = -> Fusion075 [Edge125]
  Edges = 1 edges r=2: [Edge125]
FEATURE [Part::Fillet] Fillet048
  Base = -> Fillet047
  EdgeLinks = -> Fillet047 [Edge136]
  Edges = 1 edges r=2: [Edge136]
FEATURE [Part::MultiFuse] Fusion076
  Shapes = -> [Fillet048,Fillet007]
FEATURE [Part::Chamfer] Chamfer  label="BaseSup002"
  Base = -> Fusion076
  EdgeLinks = -> Fusion076 [Edge137]
  Edges = 1 edges r=2: [Edge137]
FEATURE [Part::Cut] Cut119
  Base = -> Chamfer
  Tool = -> Fillet049
FEATURE [Part::Fillet] Fillet050  label="BaseSup003"
  Base = -> Cut119
  EdgeLinks = -> Cut119 [Edge41,Edge45]
  Edges = 2 edges r=1: [Edge41,Edge45]
FEATURE [Part::Cut] Cut147  label="BaseInf007"
  Base = -> Fillet050
  Tool = -> Box128
FEATURE [Part::Cut] Cut148
  Base = -> Cut147
  Tool = -> Box129
FEATURE [Part::Cut] Cut151  label="BaseSup004"
  Base = -> Cut148
  Tool = -> Box134
FEATURE [Part::MultiFuse] Fusion085
  Shapes = -> [Cut151,Fillet084]
FEATURE [Part::MultiFuse] Fusion086
  Shapes = -> [Fusion085,Fillet082]
FEATURE [Part::MultiFuse] Fusion087  label="BaseSup005"
  Shapes = -> [Fusion086,Fillet080]
FEATURE [Part::Cut] Cut235
  Base = -> Fusion087
  Tool = -> Box184
FEATURE [Part::Fillet] Fillet141
  Base = -> Cut235
  EdgeLinks = -> Cut235 [Edge15]
  Edges = 1 edges r=2.5: [Edge15]
FEATURE [Part::Fillet] Fillet142
  Base = -> Fillet141
  EdgeLinks = -> Fillet141 [Edge97]
  Edges = 1 edges r=2.5: [Edge97]
FEATURE [Part::Fillet] Fillet143
  Base = -> Fillet142
  EdgeLinks = -> Fillet142 [Edge20]
  Edges = 1 edges r=2.5: [Edge20]
FEATURE [Part::Fillet] Fillet144  label="BloquComponentes"
  Base = -> Fillet143
  EdgeLinks = -> Fillet143 [Edge92]
  Edges = 1 edges r=2.5: [Edge92]
FEATURE [Part::MultiFuse] Fusion103
  Shapes = -> [Fillet144,Cylinder158]
FEATURE [Part::MultiFuse] Fusion104
  Shapes = -> [Fusion103,Cylinder161]
FEATURE [Part::MultiFuse] Fusion105
  Shapes = -> [Fusion104,Cylinder160]
FEATURE [Part::MultiFuse] Fusion106
  Shapes = -> [Fusion105,Cylinder159]
FEATURE [Part::MultiFuse] Fusion107
  Shapes = -> [Fusion106,Fillet146]
FEATURE [Part::MultiFuse] Fusion108
  Shapes = -> [Fusion107,Fillet148]
FEATURE [Part::Offset] Offset002
  Fill = false
  Intersection = false
  Join = 0
  Mode = 0
  SelfIntersection = false
  Source = -> Box
  Value = 0.2
FEATURE [Part::Cut] Cut114  label="Lateral_De003"
  Base = -> Fusion074
  Tool = -> Offset002
FEATURE [Part::Cut] Cut177
  Base = -> Cut114
  Tool = -> Box165
FEATURE [Part::Cut] Cut179
  Base = -> Cut177
  Tool = -> Box167
FEATURE [Part::Cut] Cut181
  Base = -> Cut179
  Tool = -> Cylinder110
FEATURE [Part::Cut] Cut182
  Base = -> Cut181
  Tool = -> Cylinder111
FEATURE [Part::Cut] Cut183
  Base = -> Cut182
  Tool = -> Cylinder112
FEATURE [Part::Cut] Cut184
  Base = -> Cut183
  Tool = -> Cylinder120
FEATURE [Part::Cut] Cut185
  Base = -> Cut184
  Tool = -> Cylinder119
FEATURE [Part::Cut] Cut186
  Base = -> Cut185
  Tool = -> Cylinder118
FEATURE [Part::Cut] Cut187
  Base = -> Cut186
  Tool = -> Cylinder117
FEATURE [Part::Cut] Cut188
  Base = -> Cut187
  Tool = -> Cylinder116
FEATURE [Part::Cut] Cut189
  Base = -> Cut188
  Tool = -> Cylinder115
FEATURE [Part::Cut] Cut190
  Base = -> Cut189
  Tool = -> Cylinder114
FEATURE [Part::Cut] Cut191  label="LateralDer"
  Base = -> Cut190
  Tool = -> Cylinder113
FEATURE [Part::Cut] Cut202
  Base = -> Cut191
  Tool = -> Box168
FEATURE [Part::Cut] Cut203  label="LateralDer001"
  Base = -> Cut202
  Tool = -> Box169
FEATURE [Part::Cut] Cut255  label="LateralDer002"
  Base = -> Cut203
  Tool = -> Box197
FEATURE [Part::Cut] Cut256  label="LateralDer003"
  Base = -> Cut255
  Tool = -> Box198
FEATURE [Part::Offset] Offset003
  Fill = false
  Intersection = false
  Join = 0
  Mode = 0
  SelfIntersection = false
  Source = -> Box102
  Value = 0.2
FEATURE [Part::Cut] Cut113  label="Lateral_Iz003"
  Base = -> Cut099
  Tool = -> Offset003
FEATURE [Part::Cut] Cut178
  Base = -> Cut113
  Tool = -> Box166
FEATURE [Part::Cut] Cut180
  Base = -> Cut178
  Tool = -> Cylinder109
FEATURE [Part::Cut] Cut192
  Base = -> Cut180
  Tool = -> Cylinder121
FEATURE [Part::Cut] Cut193
  Base = -> Cut192
  Tool = -> Cylinder130
FEATURE [Part::Cut] Cut194
  Base = -> Cut193
  Tool = -> Cylinder129
FEATURE [Part::MultiFuse] Fusion095
  Shapes = -> [Cut194,Cylinder128]
FEATURE [Part::Cut] Cut195
  Base = -> Fusion095
  Tool = -> Cylinder127
FEATURE [Part::Cut] Cut196
  Base = -> Cut195
  Tool = -> Cylinder126
FEATURE [Part::Cut] Cut197
  Base = -> Cut196
  Tool = -> Cylinder125
FEATURE [Part::Cut] Cut198
  Base = -> Cut197
  Tool = -> Cylinder124
FEATURE [Part::Cut] Cut199
  Base = -> Cut198
  Tool = -> Cylinder123
FEATURE [Part::Cut] Cut200
  Base = -> Cut199
  Tool = -> Cylinder122
FEATURE [Part::Cut] Cut201  label="LateralIzq"
  Base = -> Cut200
  Tool = -> Cylinder131
FEATURE [Part::Offset] Offset004
  Fill = false
  Intersection = false
  Join = 0
  Mode = 0
  SelfIntersection = false
  Source = -> Box112
  Value = 0.2
FEATURE [Part::Cut] Cut123  label="Lateral_Iz005"
  Base = -> Cut122
  Tool = -> Offset004
FEATURE [Part::Cut] Cut138
  Base = -> Cut096
  Tool = -> Cut123
FEATURE [Part::Offset] Offset005
  Fill = false
  Intersection = false
  Join = 0
  Mode = 0
  SelfIntersection = false
  Source = -> Box113
  Value = 0.2
FEATURE [Part::Cut] Cut137  label="Lateral_De004"
  Base = -> Fusion083
  Tool = -> Offset005
FEATURE [Part::Cut] Cut139  label="BaseInf004"
  Base = -> Cut138
  Tool = -> Cut137
FEATURE [Part::Offset] Offset006
  Fill = false
  Intersection = false
  Join = 0
  Mode = 0
  SelfIntersection = false
  Source = -> Fillet063
  Value = 0.2
FEATURE [Part::Cut] Cut140
  Base = -> Cut139
  Tool = -> Offset006
FEATURE [Part::Offset] Offset007
  Fill = false
  Intersection = false
  Join = 0
  Mode = 0
  Placement = pos=(56,0,0) rot=(0,0,1;0rad)
  SelfIntersection = false
  Source = -> Fillet065
  Value = 0.2
FEATURE [Part::Cut] Cut141
  Base = -> Cut140
  Tool = -> Offset007
FEATURE [Part::Fillet] Fillet066
  Base = -> Cut141
  EdgeLinks = -> Cut141 [Edge55,Edge56,Edge57,Edge58,Edge59,Edge60,Edge61]
  Edges = 7 edges r=1: [Edge55,Edge56,Edge57,Edge58,Edge59,Edge60,Edge61]
FEATURE [Part::Fillet] Fillet067
  Base = -> Fillet066
  EdgeLinks = -> Fillet066 [Edge34,Edge38]
  Edges = 2 edges r=1: [Edge34,Edge38]
FEATURE [Part::Fillet] Fillet068  label="BaseInf005"
  Base = -> Fillet067
  EdgeLinks = -> Fillet067 [Edge28,Edge32]
  Edges = 2 edges r=1: [Edge28,Edge32]
FEATURE [Part::Cut] Cut142  label="BaseInf006"
  Base = -> Fillet068
  Tool = -> Cylinder104
FEATURE [Part::Cut] Cut204  label="BaseInf009"
  Base = -> Cut142
  Tool = -> Cylinder133
FEATURE [Part::Offset] Offset010
  Fill = false
  Intersection = false
  Join = 0
  Mode = 0
  SelfIntersection = false
  Source = -> Box174
  Value = 0.2
FEATURE [Part::Cut] Cut214  label="Lateral_Iz009"
  Base = -> Cut213
  Tool = -> Offset010
FEATURE [Part::Cut] Cut229
  Base = -> Cut210
  Tool = -> Cut214
FEATURE [Part::Offset] Offset011
  Fill = false
  Intersection = false
  Join = 0
  Mode = 0
  SelfIntersection = false
  Source = -> Box175
  Value = 0.2
FEATURE [Part::Cut] Cut228  label="Lateral_De008"
  Base = -> Fusion102
  Tool = -> Offset011
FEATURE [Part::Cut] Cut230  label="BaseInf014"
  Base = -> Cut229
  Tool = -> Cut228
FEATURE [Part::Offset] Offset012
  Fill = false
  Intersection = false
  Join = 0
  Mode = 0
  SelfIntersection = false
  Source = -> Fillet135
  Value = 0.2
FEATURE [Part::Cut] Cut231
  Base = -> Cut230
  Tool = -> Offset012
FEATURE [Part::Offset] Offset013
  Fill = false
  Intersection = false
  Join = 0
  Mode = 0
  Placement = pos=(56,0,0) rot=(0,0,1;0rad)
  SelfIntersection = false
  Source = -> Fillet137
  Value = 0.2
FEATURE [Part::Cut] Cut232
  Base = -> Cut231
  Tool = -> Offset013
FEATURE [Part::Fillet] Fillet138
  Base = -> Cut232
  EdgeLinks = -> Cut232 [Edge55,Edge56,Edge57,Edge58,Edge59,Edge60,Edge61]
  Edges = 7 edges r=1: [Edge55,Edge56,Edge57,Edge58,Edge59,Edge60,Edge61]
FEATURE [Part::Fillet] Fillet139
  Base = -> Fillet138
  EdgeLinks = -> Fillet138 [Edge34,Edge38]
  Edges = 2 edges r=1: [Edge34,Edge38]
FEATURE [Part::Fillet] Fillet140  label="BaseInf017"
  Base = -> Fillet139
  EdgeLinks = -> Fillet139 [Edge28,Edge32]
  Edges = 2 edges r=1: [Edge28,Edge32]
FEATURE [Part::Cut] Cut233  label="BaseInf015"
  Base = -> Fillet140
  Tool = -> Cylinder156
FEATURE [Part::Cut] Cut234  label="BaseSup012"
  Base = -> Cut233
  Placement = pos=(0,0,105) rot=(0,0,1;0rad)
  Tool = -> Cylinder157
FEATURE [Part::MultiFuse] Fusion109  label="BaseSup013"
  Shapes = -> [Cut234,Fusion108]
FEATURE [Part::MultiFuse] Fusion178  label="Capsula_Paracaidas"
  Shapes = -> [Cut201,Cut204,Fusion109,Cut256]
